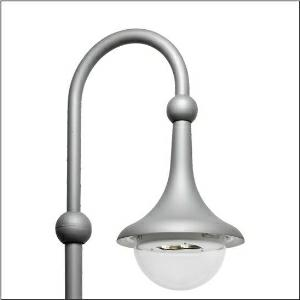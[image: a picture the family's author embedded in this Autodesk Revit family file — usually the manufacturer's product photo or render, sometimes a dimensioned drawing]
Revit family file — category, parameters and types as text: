
# Revit family: grosse_glocke___st1_2a_5xa1563k1b108_1a11
name_source: partatom
category: Lighting Fixtures
units: mm (PartAtom-declared; Revit-internal decimal feet)

## family parameters
Cut with Voids When Loaded = No
Host = Face
Light Source = No
Part Type = Normal
Room Calculation Point = No
Round Connector Dimension = Use Diameter
Shared = No

## types (1)
- --- (1 x LED, 3320 lm, 23.4 W, 4000K)
    Apparent Load = 23 VA
    CIE Flux Codes = 29 66 95 99 100
    Color Rendering = 70
    Color Temperature = 4000K
    Default Elevation = 1800 mm
    Description = Large Bell, mast luminaire, primary light control with 3 zone facetted reflector, of plastic, silver coated, primary optical cover: enclosure, of PMMA, transparent, light distribution: ST1.2a, light emission: direct distribution, primary light characteristic: asymmetric, installation type: suspended mounting, LED High Power LED, rated luminous flux: 3.320 lm, light colour: 740, colour temperature: 4000K, control gear: ECG Plus, control: flexible luminous flux parameterisation, time-dependent luminous flux control, constant luminous flux control, digital communication interface, power reduction, electronic power reduction, mains connection: 220..240V, AC, 50/60Hz, start of lifetime: 23 W, end of lifetime: 24 W, reduction: 12 W, luminaire housing, bell-shaped, of glass-fibre reinforced polyester, coated, Siteco® metallic grey (DB 702S), diameter: 530 mm, height: 695mm, protection rating (complete): IP54, insulation class (complete): insulation class II (safety insulation), certification: CE, ENEC, VDE, impact resistance: IK08, standard-compliant lighting for roads and squares, packaging unit: 1 piece

Light Distribution: ST1.2a
    Height = 695 mm
    Lamp = 1 x LED
    Lamp Light Flux = 3320 lm
    Lamp Power = 23.4 W
    Lamp count = 1
    Length = 530 mm
    Luminous efficacy = 142 lm/W
    Manufacturer = Siteco
    ModVariant = No
    Model = 5XA1563K1B108
    Number of Poles = 1
    OnlyDefault = Yes
    Power Factor = 1
    Product Name = Große Glocke | ST1.2a
    Product group = mast luminaire | pylon annexe
    ProductGroupID = 6200
    Protection Class = Protection class II
    Protection Degree = IP 54
    RLX_Detail_Level = 1
    RlxData = <blob elided: 52517 chars, md5=59691146>
    Socket = socket
    Standby Power = 0 W
    System Light Flux = 3320 lm
    System Power = 23 W
    Type Comments = factory setting: luminous flux: 100 % | dim-lin: 254 | 460 mA
    Type Image = l_1005953.jpg
    URL = http://relux.com
    VarID = @adj_130613
    Voltage = 0 V
    Weight = 0.00 kg
    Width = 0 mm  [stored 0 ft]

note: [stored X ft] marks values corroborated as IEEE doubles in the binary element streams (Revit-internal decimal feet)

## geometry (parser evidence)
native form markers: Blend x4, Sweep x10
no freeform markers — native parametric forms only
